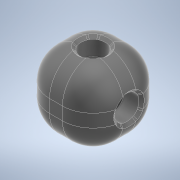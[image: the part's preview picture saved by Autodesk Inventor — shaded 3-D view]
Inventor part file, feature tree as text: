
AUTODESK INVENTOR PART (.ipt)
format: ipt  version: 2022 (Build 260153000, 153)  size: 444,928 bytes
history: native  units: in
note: dims shown in document units (in); Inventor stores cm internally (conversion verified against a paired STEP export)
features: sketch x4, extrude x2, fillet x1, hole x1, other x1, pattern_circular x1, chamfer x1
ambient origin geometry x8: Origin, YZ Plane, XZ Plane, XY Plane, X Axis, Y Axis, Z Axis, Center Point
bodies: Body1 (feature_tree)
feature tree (11):
  extrude  "Extrusion2"  Depth=0.4764in
  fillet  "Fillet2"  Radius=0.4764in
  hole  "Hole1"  [1 undecoded]
  sketch  "Sketch5"  dims[d11=0.1575in d12=0.2362in d13=0.1575in d14=0.0787in d15=90.0deg d16=0.1181in d17=0.0in d18=0.2382in]
  other  "Work Axis6"
  pattern_circular  "Circular Pattern1"  [2 undecoded]
  chamfer  "Chamfer3"  Distance=0.0413in
  extrude  "Extrusion3"  Depth=1.5748in TaperAngle=360.0deg
  sketch  "Sketch3"  dims[d6=0.4764in d7=0.4764in d8=0.4764in d9=0.0in]
  sketch  "Sketch4"  dims[d10=0.1969in]
  sketch  "Sketch6"  dims[d19=0.2382in d20=0.0413in d21=0.0413in d22=1.5748in d23=360.0deg d31=0.0197in d32=0.0787in d33=45.0deg d34=0.4764in d35=0.4764in d36=0.0394in d37=0.0in]
note: 3 required parameter values undecoded (feature->parameter linkage not recoverable at this tier; creation-order binding heuristic only, values carry confidence <= 0.55)
